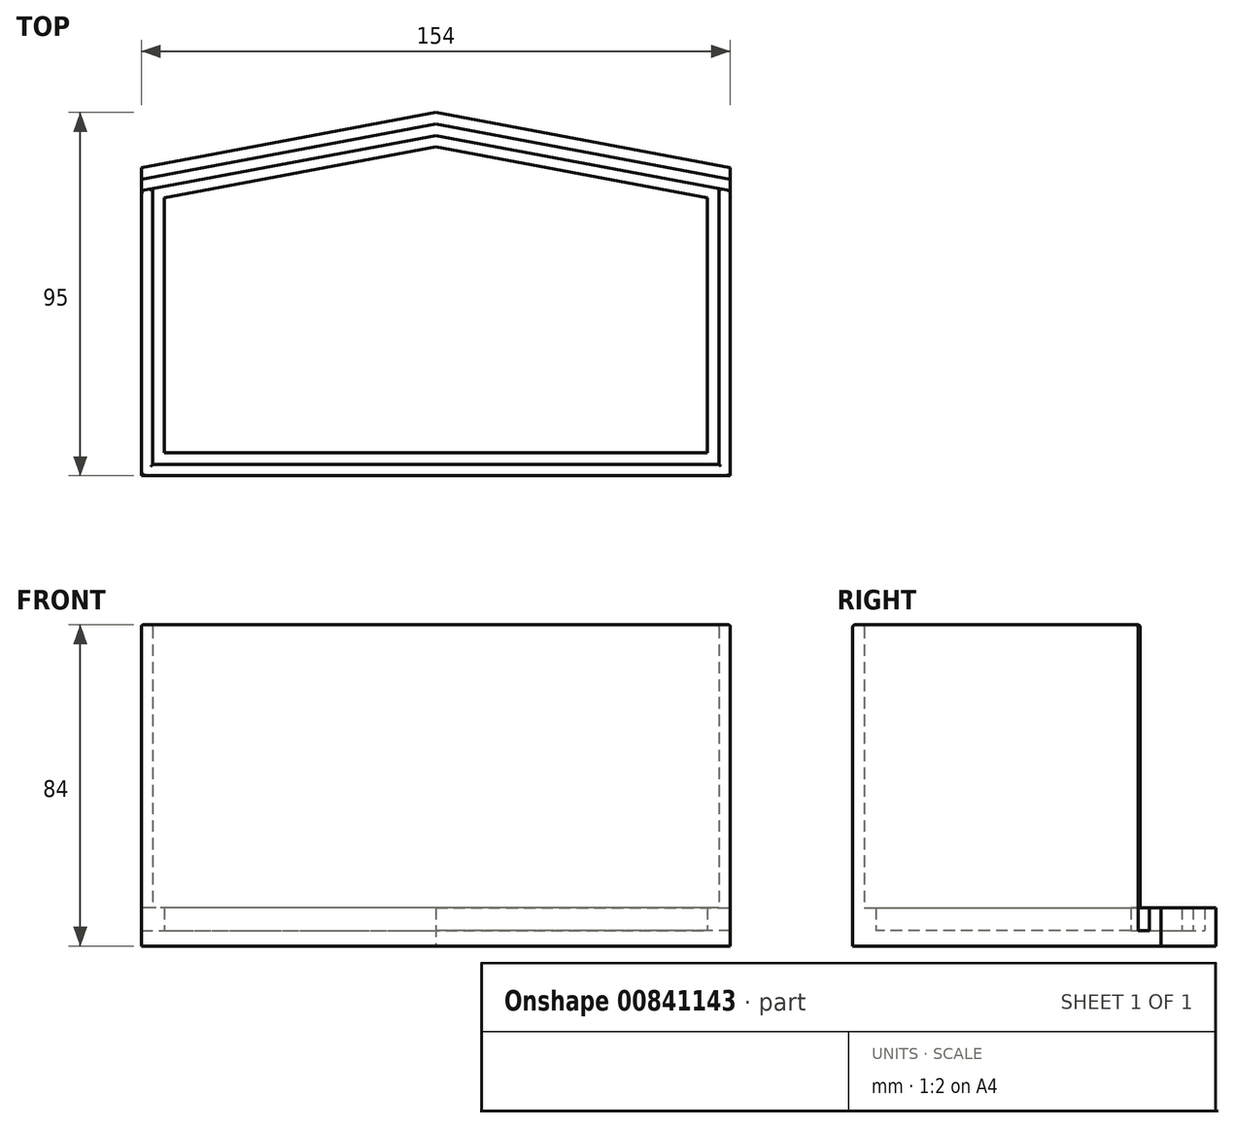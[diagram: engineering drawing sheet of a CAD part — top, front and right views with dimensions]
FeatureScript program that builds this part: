
annotation { "Feature Type Name" : "Feature", "Feature Type Description" : "" }
export const myFeature = defineFeature(function(context is Context, id is Id, definition is map)
    precondition{}
    {
        {
            var Q0;
            Q0=qCreatedBy(makeId("Top.planeOp"),FACE);
            var sketch = newSketch(context, id + "F0", { "sketchPlane" : qUnion([Q0])});
            skLineSegment(sketch, "E0.bottom", {"start": v(80, -49) * mm, "end": v(-80, -49) * mm});
            skLineSegment(sketch, "E0.top", {"start": v(80, 49) * mm, "end": v(-80, 49) * mm, "construction": true});
            skLineSegment(sketch, "E0.left", {"start": v(80, -49) * mm, "end": v(80, 49) * mm});
            skLineSegment(sketch, "E0.right", {"start": v(-80, -49) * mm, "end": v(-80, 49) * mm});
            skPoint(sketch, "E0.middle", {"position": v(0, 0) * mm});
            skLineSegment(sketch, "E1.bottom", {"start": v(-80, -49) * mm, "end": v(80, -49) * mm});
            skLineSegment(sketch, "E1.left", {"start": v(-80, -49) * mm, "end": v(-80, 85) * mm});
            skLineSegment(sketch, "E1.right", {"start": v(80, -49) * mm, "end": v(80, 43) * mm});
            skLineSegment(sketch, "E2.bottom", {"start": v(77, -46) * mm, "end": v(-77, -46) * mm});
            skLineSegment(sketch, "E2.top", {"start": v(77, 46) * mm, "end": v(-77, 46) * mm, "construction": true});
            skLineSegment(sketch, "E2.left", {"start": v(77, -46) * mm, "end": v(77, 46) * mm});
            skLineSegment(sketch, "E2.right", {"start": v(-77, -46) * mm, "end": v(-77, 46) * mm});
            skLineSegment(sketch, "E3.bottom", {"start": v(74, -43) * mm, "end": v(-74, -43) * mm});
            skLineSegment(sketch, "E3.top", {"start": v(74, 43) * mm, "end": v(-74, 43) * mm, "construction": true});
            skLineSegment(sketch, "E3.left", {"start": v(74, -43) * mm, "end": v(74, 43) * mm});
            skLineSegment(sketch, "E3.right", {"start": v(-74, -43) * mm, "end": v(-74, 43) * mm});
            skLineSegment(sketch, "E4.bottom", {"start": v(71, -40) * mm, "end": v(-71, -40) * mm});
            skLineSegment(sketch, "E4.top", {"start": v(71, 40) * mm, "end": v(-71, 40) * mm, "construction": true});
            skLineSegment(sketch, "E4.left", {"start": v(71, -40) * mm, "end": v(71, 40) * mm});
            skLineSegment(sketch, "E4.right", {"start": v(-71, -40) * mm, "end": v(-71, 40) * mm});
            skLineSegment(sketch, "E5.bottom", {"start": v(-80, 49) * mm, "end": v(80, 49) * mm, "construction": true});
            skLineSegment(sketch, "E5.top", {"start": v(-80, 34) * mm, "end": v(80, 34) * mm, "construction": true});
            skLineSegment(sketch, "E5.left", {"start": v(-80, 49) * mm, "end": v(-80, 34) * mm, "construction": true});
            skLineSegment(sketch, "E5.right", {"start": v(80, 49) * mm, "end": v(80, 34) * mm, "construction": true});
            skLineSegment(sketch, "E6", {"start": v(0, 49) * mm, "end": v(0, -49) * mm, "construction": true});
            skLineSegment(sketch, "E7", {"start": v(0, 49) * mm, "end": v(-80, 34) * mm});
            skLineSegment(sketch, "E8", {"start": v(0, 46) * mm, "end": v(-80, 31) * mm});
            skLineSegment(sketch, "E9", {"start": v(0, 43) * mm, "end": v(-80, 28) * mm});
            skLineSegment(sketch, "E10", {"start": v(0, 40) * mm, "end": v(-80, 25) * mm});
            skLineSegment(sketch, "E11", {"start": v(0, 49) * mm, "end": v(80, 34) * mm});
            skLineSegment(sketch, "E12", {"start": v(0, 46) * mm, "end": v(80, 31) * mm});
            skLineSegment(sketch, "E13", {"start": v(0, 43) * mm, "end": v(80, 28) * mm});
            skLineSegment(sketch, "E14", {"start": v(0, 40) * mm, "end": v(80, 25) * mm});
            skSolve(sketch);
        }
        {
            var Q0;
            {var subQ6=sQuery(id+"F0.wireOp",EDGE,"E4.bottom");Q0=makeQuery(id+"F0.imprint","IMPRINT",FACE,{"disambiguationData":[TD([[makeQuery(id+"F0.imprint","IMPRINT",EDGE,{"derivedFrom":subQ6}),-1.0]])]});}
            var Q1;
            {var subQ2=sQuery(id+"F0.wireOp",EDGE,"E2.bottom");Q1=makeQuery(id+"F0.imprint","IMPRINT",FACE,{"disambiguationData":[TD([[makeQuery(id+"F0.imprint","IMPRINT",EDGE,{"derivedFrom":subQ2}),-1.0]])]});}
            var Q2;
            {var subQ0=sQuery(id+"F0.wireOp",EDGE,"E13");var subQ9=sQuery(id+"F0.wireOp",EDGE,"E4.left");var subQ11=makeQuery(id+"F0.imprint","INTERSECT",VERTEX,{"derivedFrom":[subQ9,subQ0]});Q2=makeQuery(id+"F0.imprint","IMPRINT",FACE,{"disambiguationData":[TD([[makeQuery(id+"F0.imprint","IMPRINT",EDGE,{"disambiguationData":[TD([[subQ11,-1.0]])],"derivedFrom":subQ9}),1.0]])]});}
            var Q3;
            {var subQ2=sQuery(id+"F0.wireOp",EDGE,"E1.bottom");Q3=makeQuery(id+"F0.imprint","IMPRINT",FACE,{"disambiguationData":[TD([[makeQuery(id+"F0.imprint","IMPRINT",EDGE,{"derivedFrom":subQ2}),1.0]])]});}
            var Q4;
            {var subQ7=sQuery(id+"F0.wireOp",EDGE,"E3.bottom");Q4=makeQuery(id+"F0.imprint","IMPRINT",FACE,{"disambiguationData":[TD([[makeQuery(id+"F0.imprint","IMPRINT",EDGE,{"derivedFrom":subQ7}),-1.0]])]});}
            var Q5;
            {var subQ0=sQuery(id+"F0.wireOp",EDGE,"E8");var subQ1=sQuery(id+"F0.wireOp",EDGE,"E1.left");var subQ2=makeQuery(id+"F0.imprint","INTERSECT",VERTEX,{"derivedFrom":[subQ1,subQ0]});Q5=makeQuery(id+"F0.imprint","IMPRINT",FACE,{"disambiguationData":[TD([[makeQuery(id+"F0.imprint","IMPRINT",EDGE,{"disambiguationData":[TD([[subQ2,1.0]])],"derivedFrom":subQ1}),-1.0]])]});}
            var Q6;
            {var subQ0=sQuery(id+"F0.wireOp",EDGE,"E7");var subQ1=sQuery(id+"F0.wireOp",EDGE,"E1.left");var subQ2=makeQuery(id+"F0.imprint","INTERSECT",VERTEX,{"derivedFrom":[subQ1,subQ0]});Q6=makeQuery(id+"F0.imprint","IMPRINT",FACE,{"disambiguationData":[TD([[makeQuery(id+"F0.imprint","IMPRINT",EDGE,{"disambiguationData":[TD([[subQ2,1.0]])],"derivedFrom":subQ1}),-1.0]])]});}
            var Q7;
            {var subQ0=sQuery(id+"F0.wireOp",EDGE,"E9");var subQ1=sQuery(id+"F0.wireOp",EDGE,"E1.left");var subQ2=makeQuery(id+"F0.imprint","INTERSECT",VERTEX,{"derivedFrom":[subQ1,subQ0]});Q7=makeQuery(id+"F0.imprint","IMPRINT",FACE,{"disambiguationData":[TD([[makeQuery(id+"F0.imprint","IMPRINT",EDGE,{"disambiguationData":[TD([[subQ2,1.0]])],"derivedFrom":subQ1}),-1.0]])]});}
            var Q8;
            {var subQ0=sQuery(id+"F0.wireOp",EDGE,"E7");var subQ1=sQuery(id+"F0.wireOp",EDGE,"E2.right");var subQ2=makeQuery(id+"F0.imprint","INTERSECT",VERTEX,{"derivedFrom":[subQ1,subQ0]});Q8=makeQuery(id+"F0.imprint","IMPRINT",FACE,{"disambiguationData":[TD([[makeQuery(id+"F0.imprint","IMPRINT",EDGE,{"disambiguationData":[TD([[subQ2,1.0]])],"derivedFrom":subQ1}),-1.0]])]});}
            var Q9;
            {var subQ0=sQuery(id+"F0.wireOp",EDGE,"E9");var subQ1=sQuery(id+"F0.wireOp",EDGE,"E2.right");var subQ2=makeQuery(id+"F0.imprint","INTERSECT",VERTEX,{"derivedFrom":[subQ1,subQ0]});Q9=makeQuery(id+"F0.imprint","IMPRINT",FACE,{"disambiguationData":[TD([[makeQuery(id+"F0.imprint","IMPRINT",EDGE,{"disambiguationData":[TD([[subQ2,-1.0]])],"derivedFrom":subQ1}),-1.0]])]});}
            var Q10;
            {var subQ0=sQuery(id+"F0.wireOp",EDGE,"E10");var subQ1=sQuery(id+"F0.wireOp",EDGE,"E2.right");var subQ2=makeQuery(id+"F0.imprint","INTERSECT",VERTEX,{"derivedFrom":[subQ1,subQ0]});Q10=makeQuery(id+"F0.imprint","IMPRINT",FACE,{"disambiguationData":[TD([[makeQuery(id+"F0.imprint","IMPRINT",EDGE,{"disambiguationData":[TD([[subQ2,-1.0]])],"derivedFrom":subQ1}),-1.0]])]});}
            var Q11;
            {var subQ0=sQuery(id+"F0.wireOp",EDGE,"E9");var subQ1=sQuery(id+"F0.wireOp",EDGE,"E3.right");var subQ2=makeQuery(id+"F0.imprint","INTERSECT",VERTEX,{"derivedFrom":[subQ1,subQ0]});Q11=makeQuery(id+"F0.imprint","IMPRINT",FACE,{"disambiguationData":[TD([[makeQuery(id+"F0.imprint","IMPRINT",EDGE,{"disambiguationData":[TD([[subQ2,-1.0]])],"derivedFrom":subQ1}),-1.0]])]});}
            var Q12;
            {var subQ0=sQuery(id+"F0.wireOp",EDGE,"E10");var subQ1=sQuery(id+"F0.wireOp",EDGE,"E3.right");var subQ2=makeQuery(id+"F0.imprint","INTERSECT",VERTEX,{"derivedFrom":[subQ1,subQ0]});Q12=makeQuery(id+"F0.imprint","IMPRINT",FACE,{"disambiguationData":[TD([[makeQuery(id+"F0.imprint","IMPRINT",EDGE,{"disambiguationData":[TD([[subQ2,-1.0]])],"derivedFrom":subQ1}),-1.0]])]});}
            var Q13;
            {var subQ0=sQuery(id+"F0.wireOp",EDGE,"E7");var subQ1=sQuery(id+"F0.wireOp",EDGE,"E3.right");var subQ2=makeQuery(id+"F0.imprint","INTERSECT",VERTEX,{"derivedFrom":[subQ1,subQ0]});Q13=makeQuery(id+"F0.imprint","IMPRINT",FACE,{"disambiguationData":[TD([[makeQuery(id+"F0.imprint","IMPRINT",EDGE,{"disambiguationData":[TD([[subQ2,1.0]])],"derivedFrom":subQ1}),-1.0]])]});}
            var Q14;
            {var subQ7=sQuery(id+"F0.wireOp",EDGE,"E11");var subQ9=sQuery(id+"F0.wireOp",EDGE,"E4.left");var subQ10=makeQuery(id+"F0.imprint","INTERSECT",VERTEX,{"derivedFrom":[subQ9,subQ7]});Q14=makeQuery(id+"F0.imprint","IMPRINT",FACE,{"disambiguationData":[TD([[makeQuery(id+"F0.imprint","IMPRINT",EDGE,{"disambiguationData":[TD([[subQ10,1.0]])],"derivedFrom":subQ9}),1.0]])]});}
            var Q15;
            {var subQ0=sQuery(id+"F0.wireOp",EDGE,"E14");var subQ9=sQuery(id+"F0.wireOp",EDGE,"E4.left");var subQ10=makeQuery(id+"F0.imprint","INTERSECT",VERTEX,{"derivedFrom":[subQ9,subQ0]});Q15=makeQuery(id+"F0.imprint","IMPRINT",FACE,{"disambiguationData":[TD([[makeQuery(id+"F0.imprint","IMPRINT",EDGE,{"disambiguationData":[TD([[subQ10,-1.0]])],"derivedFrom":subQ9}),1.0]])]});}
            var Q16;
            {var subQ0=sQuery(id+"F0.wireOp",EDGE,"E11");var subQ1=sQuery(id+"F0.wireOp",EDGE,"E3.left");var subQ2=makeQuery(id+"F0.imprint","INTERSECT",VERTEX,{"derivedFrom":[subQ1,subQ0]});Q16=makeQuery(id+"F0.imprint","IMPRINT",FACE,{"disambiguationData":[TD([[makeQuery(id+"F0.imprint","IMPRINT",EDGE,{"disambiguationData":[TD([[subQ2,1.0]])],"derivedFrom":subQ1}),1.0]])]});}
            var Q17;
            {var subQ0=sQuery(id+"F0.wireOp",EDGE,"E11");var subQ1=sQuery(id+"F0.wireOp",EDGE,"E2.left");var subQ2=makeQuery(id+"F0.imprint","INTERSECT",VERTEX,{"derivedFrom":[subQ1,subQ0]});Q17=makeQuery(id+"F0.imprint","IMPRINT",FACE,{"disambiguationData":[TD([[makeQuery(id+"F0.imprint","IMPRINT",EDGE,{"disambiguationData":[TD([[subQ2,1.0]])],"derivedFrom":subQ1}),1.0]])]});}
            var Q18;
            {var subQ0=sQuery(id+"F0.wireOp",EDGE,"E11");var subQ1=sQuery(id+"F0.wireOp",EDGE,"E1.right");var subQ2=makeQuery(id+"F0.imprint","INTERSECT",VERTEX,{"derivedFrom":[subQ1,subQ0]});Q18=makeQuery(id+"F0.imprint","IMPRINT",FACE,{"disambiguationData":[TD([[makeQuery(id+"F0.imprint","IMPRINT",EDGE,{"disambiguationData":[TD([[subQ2,1.0]])],"derivedFrom":subQ1}),1.0]])]});}
            var Q19;
            {var subQ0=sQuery(id+"F0.wireOp",EDGE,"E12");var subQ1=sQuery(id+"F0.wireOp",EDGE,"E1.right");var subQ2=makeQuery(id+"F0.imprint","INTERSECT",VERTEX,{"derivedFrom":[subQ1,subQ0]});Q19=makeQuery(id+"F0.imprint","IMPRINT",FACE,{"disambiguationData":[TD([[makeQuery(id+"F0.imprint","IMPRINT",EDGE,{"disambiguationData":[TD([[subQ2,1.0]])],"derivedFrom":subQ1}),1.0]])]});}
            var Q20;
            {var subQ0=sQuery(id+"F0.wireOp",EDGE,"E13");var subQ1=sQuery(id+"F0.wireOp",EDGE,"E1.right");var subQ2=makeQuery(id+"F0.imprint","INTERSECT",VERTEX,{"derivedFrom":[subQ1,subQ0]});Q20=makeQuery(id+"F0.imprint","IMPRINT",FACE,{"disambiguationData":[TD([[makeQuery(id+"F0.imprint","IMPRINT",EDGE,{"disambiguationData":[TD([[subQ2,1.0]])],"derivedFrom":subQ1}),1.0]])]});}
            var Q21;
            {var subQ0=sQuery(id+"F0.wireOp",EDGE,"E14");var subQ1=sQuery(id+"F0.wireOp",EDGE,"E2.left");var subQ2=makeQuery(id+"F0.imprint","INTERSECT",VERTEX,{"derivedFrom":[subQ1,subQ0]});Q21=makeQuery(id+"F0.imprint","IMPRINT",FACE,{"disambiguationData":[TD([[makeQuery(id+"F0.imprint","IMPRINT",EDGE,{"disambiguationData":[TD([[subQ2,-1.0]])],"derivedFrom":subQ1}),1.0]])]});}
            var Q22;
            {var subQ0=sQuery(id+"F0.wireOp",EDGE,"E14");var subQ1=sQuery(id+"F0.wireOp",EDGE,"E3.left");var subQ2=makeQuery(id+"F0.imprint","INTERSECT",VERTEX,{"derivedFrom":[subQ1,subQ0]});Q22=makeQuery(id+"F0.imprint","IMPRINT",FACE,{"disambiguationData":[TD([[makeQuery(id+"F0.imprint","IMPRINT",EDGE,{"disambiguationData":[TD([[subQ2,-1.0]])],"derivedFrom":subQ1}),1.0]])]});}
            var Q23;
            {var subQ0=sQuery(id+"F0.wireOp",EDGE,"E13");var subQ1=sQuery(id+"F0.wireOp",EDGE,"E3.left");var subQ2=makeQuery(id+"F0.imprint","INTERSECT",VERTEX,{"derivedFrom":[subQ1,subQ0]});Q23=makeQuery(id+"F0.imprint","IMPRINT",FACE,{"disambiguationData":[TD([[makeQuery(id+"F0.imprint","IMPRINT",EDGE,{"disambiguationData":[TD([[subQ2,-1.0]])],"derivedFrom":subQ1}),1.0]])]});}
            var Q24;
            {var subQ0=sQuery(id+"F0.wireOp",EDGE,"E13");var subQ1=sQuery(id+"F0.wireOp",EDGE,"E2.left");var subQ2=makeQuery(id+"F0.imprint","INTERSECT",VERTEX,{"derivedFrom":[subQ1,subQ0]});Q24=makeQuery(id+"F0.imprint","IMPRINT",FACE,{"disambiguationData":[TD([[makeQuery(id+"F0.imprint","IMPRINT",EDGE,{"disambiguationData":[TD([[subQ2,-1.0]])],"derivedFrom":subQ1}),1.0]])]});}
            extrude(context, id + "F1", {"entities" : qUnion([Q0, Q1, Q2, Q3, Q4, Q5, Q6, Q7, Q8, Q9, Q10, Q11, Q12, Q13, Q14, Q15, Q16, Q17, Q18, Q19, Q20, Q21, Q22, Q23, Q24]), "depth" : 4 * mm, "offsetDistance" : 25 * mm});
        }
        {
            var Q0;
            {var subQ0=sQuery(id+"F0.wireOp",EDGE,"E11");var subQ1=sQuery(id+"F0.wireOp",EDGE,"E1.right");var subQ2=makeQuery(id+"F0.imprint","INTERSECT",VERTEX,{"derivedFrom":[subQ1,subQ0]});Q0=makeQuery(id+"F0.imprint","IMPRINT",FACE,{"disambiguationData":[TD([[makeQuery(id+"F0.imprint","IMPRINT",EDGE,{"disambiguationData":[TD([[subQ2,1.0]])],"derivedFrom":subQ1}),1.0]])]});}
            var Q1;
            {var subQ0=sQuery(id+"F0.wireOp",EDGE,"E11");var subQ1=sQuery(id+"F0.wireOp",EDGE,"E2.left");var subQ2=makeQuery(id+"F0.imprint","INTERSECT",VERTEX,{"derivedFrom":[subQ1,subQ0]});Q1=makeQuery(id+"F0.imprint","IMPRINT",FACE,{"disambiguationData":[TD([[makeQuery(id+"F0.imprint","IMPRINT",EDGE,{"disambiguationData":[TD([[subQ2,1.0]])],"derivedFrom":subQ1}),1.0]])]});}
            var Q2;
            {var subQ0=sQuery(id+"F0.wireOp",EDGE,"E11");var subQ1=sQuery(id+"F0.wireOp",EDGE,"E3.left");var subQ2=makeQuery(id+"F0.imprint","INTERSECT",VERTEX,{"derivedFrom":[subQ1,subQ0]});Q2=makeQuery(id+"F0.imprint","IMPRINT",FACE,{"disambiguationData":[TD([[makeQuery(id+"F0.imprint","IMPRINT",EDGE,{"disambiguationData":[TD([[subQ2,1.0]])],"derivedFrom":subQ1}),1.0]])]});}
            var Q3;
            {var subQ7=sQuery(id+"F0.wireOp",EDGE,"E11");var subQ9=sQuery(id+"F0.wireOp",EDGE,"E4.left");var subQ10=makeQuery(id+"F0.imprint","INTERSECT",VERTEX,{"derivedFrom":[subQ9,subQ7]});Q3=makeQuery(id+"F0.imprint","IMPRINT",FACE,{"disambiguationData":[TD([[makeQuery(id+"F0.imprint","IMPRINT",EDGE,{"disambiguationData":[TD([[subQ10,1.0]])],"derivedFrom":subQ9}),1.0]])]});}
            var Q4;
            {var subQ0=sQuery(id+"F0.wireOp",EDGE,"E7");var subQ1=sQuery(id+"F0.wireOp",EDGE,"E3.right");var subQ2=makeQuery(id+"F0.imprint","INTERSECT",VERTEX,{"derivedFrom":[subQ1,subQ0]});Q4=makeQuery(id+"F0.imprint","IMPRINT",FACE,{"disambiguationData":[TD([[makeQuery(id+"F0.imprint","IMPRINT",EDGE,{"disambiguationData":[TD([[subQ2,1.0]])],"derivedFrom":subQ1}),-1.0]])]});}
            var Q5;
            {var subQ0=sQuery(id+"F0.wireOp",EDGE,"E7");var subQ1=sQuery(id+"F0.wireOp",EDGE,"E2.right");var subQ2=makeQuery(id+"F0.imprint","INTERSECT",VERTEX,{"derivedFrom":[subQ1,subQ0]});Q5=makeQuery(id+"F0.imprint","IMPRINT",FACE,{"disambiguationData":[TD([[makeQuery(id+"F0.imprint","IMPRINT",EDGE,{"disambiguationData":[TD([[subQ2,1.0]])],"derivedFrom":subQ1}),-1.0]])]});}
            var Q6;
            {var subQ0=sQuery(id+"F0.wireOp",EDGE,"E7");var subQ1=sQuery(id+"F0.wireOp",EDGE,"E1.left");var subQ2=makeQuery(id+"F0.imprint","INTERSECT",VERTEX,{"derivedFrom":[subQ1,subQ0]});Q6=makeQuery(id+"F0.imprint","IMPRINT",FACE,{"disambiguationData":[TD([[makeQuery(id+"F0.imprint","IMPRINT",EDGE,{"disambiguationData":[TD([[subQ2,1.0]])],"derivedFrom":subQ1}),-1.0]])]});}
            var Q7;
            {var subQ0=sQuery(id+"F0.wireOp",EDGE,"E9");var subQ1=sQuery(id+"F0.wireOp",EDGE,"E1.left");var subQ2=makeQuery(id+"F0.imprint","INTERSECT",VERTEX,{"derivedFrom":[subQ1,subQ0]});Q7=makeQuery(id+"F0.imprint","IMPRINT",FACE,{"disambiguationData":[TD([[makeQuery(id+"F0.imprint","IMPRINT",EDGE,{"disambiguationData":[TD([[subQ2,1.0]])],"derivedFrom":subQ1}),-1.0]])]});}
            var Q8;
            {var subQ0=sQuery(id+"F0.wireOp",EDGE,"E10");var subQ1=sQuery(id+"F0.wireOp",EDGE,"E2.right");var subQ2=makeQuery(id+"F0.imprint","INTERSECT",VERTEX,{"derivedFrom":[subQ1,subQ0]});Q8=makeQuery(id+"F0.imprint","IMPRINT",FACE,{"disambiguationData":[TD([[makeQuery(id+"F0.imprint","IMPRINT",EDGE,{"disambiguationData":[TD([[subQ2,-1.0]])],"derivedFrom":subQ1}),-1.0]])]});}
            var Q9;
            {var subQ0=sQuery(id+"F0.wireOp",EDGE,"E10");var subQ1=sQuery(id+"F0.wireOp",EDGE,"E3.right");var subQ2=makeQuery(id+"F0.imprint","INTERSECT",VERTEX,{"derivedFrom":[subQ1,subQ0]});Q9=makeQuery(id+"F0.imprint","IMPRINT",FACE,{"disambiguationData":[TD([[makeQuery(id+"F0.imprint","IMPRINT",EDGE,{"disambiguationData":[TD([[subQ2,-1.0]])],"derivedFrom":subQ1}),-1.0]])]});}
            var Q10;
            {var subQ0=sQuery(id+"F0.wireOp",EDGE,"E14");var subQ9=sQuery(id+"F0.wireOp",EDGE,"E4.left");var subQ10=makeQuery(id+"F0.imprint","INTERSECT",VERTEX,{"derivedFrom":[subQ9,subQ0]});Q10=makeQuery(id+"F0.imprint","IMPRINT",FACE,{"disambiguationData":[TD([[makeQuery(id+"F0.imprint","IMPRINT",EDGE,{"disambiguationData":[TD([[subQ10,-1.0]])],"derivedFrom":subQ9}),1.0]])]});}
            var Q11;
            {var subQ0=sQuery(id+"F0.wireOp",EDGE,"E13");var subQ1=sQuery(id+"F0.wireOp",EDGE,"E1.right");var subQ2=makeQuery(id+"F0.imprint","INTERSECT",VERTEX,{"derivedFrom":[subQ1,subQ0]});Q11=makeQuery(id+"F0.imprint","IMPRINT",FACE,{"disambiguationData":[TD([[makeQuery(id+"F0.imprint","IMPRINT",EDGE,{"disambiguationData":[TD([[subQ2,1.0]])],"derivedFrom":subQ1}),1.0]])]});}
            var Q12;
            {var subQ0=sQuery(id+"F0.wireOp",EDGE,"E14");var subQ1=sQuery(id+"F0.wireOp",EDGE,"E2.left");var subQ2=makeQuery(id+"F0.imprint","INTERSECT",VERTEX,{"derivedFrom":[subQ1,subQ0]});Q12=makeQuery(id+"F0.imprint","IMPRINT",FACE,{"disambiguationData":[TD([[makeQuery(id+"F0.imprint","IMPRINT",EDGE,{"disambiguationData":[TD([[subQ2,-1.0]])],"derivedFrom":subQ1}),1.0]])]});}
            var Q13;
            {var subQ0=sQuery(id+"F0.wireOp",EDGE,"E14");var subQ1=sQuery(id+"F0.wireOp",EDGE,"E3.left");var subQ2=makeQuery(id+"F0.imprint","INTERSECT",VERTEX,{"derivedFrom":[subQ1,subQ0]});Q13=makeQuery(id+"F0.imprint","IMPRINT",FACE,{"disambiguationData":[TD([[makeQuery(id+"F0.imprint","IMPRINT",EDGE,{"disambiguationData":[TD([[subQ2,-1.0]])],"derivedFrom":subQ1}),1.0]])]});}
            var Q14;
            {var subQ2=sQuery(id+"F0.wireOp",EDGE,"E1.bottom");Q14=makeQuery(id+"F0.imprint","IMPRINT",FACE,{"disambiguationData":[TD([[makeQuery(id+"F0.imprint","IMPRINT",EDGE,{"derivedFrom":subQ2}),1.0]])]});}
            var Q15;
            {var subQ7=sQuery(id+"F0.wireOp",EDGE,"E3.bottom");Q15=makeQuery(id+"F0.imprint","IMPRINT",FACE,{"disambiguationData":[TD([[makeQuery(id+"F0.imprint","IMPRINT",EDGE,{"derivedFrom":subQ7}),-1.0]])]});}
            var Q16;
            {var subQ0=sQuery(id+"F0.wireOp",EDGE,"E8");var subQ1=sQuery(id+"F0.wireOp",EDGE,"E1.left");var subQ2=makeQuery(id+"F0.imprint","INTERSECT",VERTEX,{"derivedFrom":[subQ1,subQ0]});Q16=makeQuery(id+"F0.imprint","IMPRINT",FACE,{"disambiguationData":[TD([[makeQuery(id+"F0.imprint","IMPRINT",EDGE,{"disambiguationData":[TD([[subQ2,1.0]])],"derivedFrom":subQ1}),-1.0]])]});}
            var Q17;
            {var subQ0=sQuery(id+"F0.wireOp",EDGE,"E12");var subQ1=sQuery(id+"F0.wireOp",EDGE,"E1.right");var subQ2=makeQuery(id+"F0.imprint","INTERSECT",VERTEX,{"derivedFrom":[subQ1,subQ0]});Q17=makeQuery(id+"F0.imprint","IMPRINT",FACE,{"disambiguationData":[TD([[makeQuery(id+"F0.imprint","IMPRINT",EDGE,{"disambiguationData":[TD([[subQ2,1.0]])],"derivedFrom":subQ1}),1.0]])]});}
            extrude(context, id + "F2", {"entities" : qUnion([Q0, Q1, Q2, Q3, Q4, Q5, Q6, Q7, Q8, Q9, Q10, Q11, Q12, Q13, Q14, Q15, Q16, Q17]), "operationType" : NewBodyOperationType.ADD, "depth" : 10 * mm, "offsetDistance" : 25 * mm});
        }
        {
            var Q0;
            {var subQ2=sQuery(id+"F0.wireOp",EDGE,"E2.bottom");Q0=makeQuery(id+"F0.imprint","IMPRINT",FACE,{"disambiguationData":[TD([[makeQuery(id+"F0.imprint","IMPRINT",EDGE,{"derivedFrom":subQ2}),-1.0]])]});}
            var Q1;
            {var subQ0=sQuery(id+"F0.wireOp",EDGE,"E10");var subQ1=sQuery(id+"F0.wireOp",EDGE,"E2.right");var subQ2=makeQuery(id+"F0.imprint","INTERSECT",VERTEX,{"derivedFrom":[subQ1,subQ0]});Q1=makeQuery(id+"F0.imprint","IMPRINT",FACE,{"disambiguationData":[TD([[makeQuery(id+"F0.imprint","IMPRINT",EDGE,{"disambiguationData":[TD([[subQ2,-1.0]])],"derivedFrom":subQ1}),-1.0]])]});}
            var Q2;
            {var subQ0=sQuery(id+"F0.wireOp",EDGE,"E14");var subQ1=sQuery(id+"F0.wireOp",EDGE,"E2.left");var subQ2=makeQuery(id+"F0.imprint","INTERSECT",VERTEX,{"derivedFrom":[subQ1,subQ0]});Q2=makeQuery(id+"F0.imprint","IMPRINT",FACE,{"disambiguationData":[TD([[makeQuery(id+"F0.imprint","IMPRINT",EDGE,{"disambiguationData":[TD([[subQ2,-1.0]])],"derivedFrom":subQ1}),1.0]])]});}
            extrude(context, id + "F3", {"entities" : qUnion([Q0, Q1, Q2]), "operationType" : NewBodyOperationType.ADD, "depth" : 84 * mm, "offsetDistance" : 25 * mm});
        }
        {
            var Q0;
            Q0=makeQuery(id+"F3.opExtrude","CAP_FACE",FACE,{"disambiguationData":[OSD([sQuery(id+"F0.wireOp",EDGE,"E2.bottom"),sQuery(id+"F0.wireOp",EDGE,"E2.left"),sQuery(id+"F0.wireOp",EDGE,"E2.right"),sQuery(id+"F0.wireOp",EDGE,"E3.bottom"),sQuery(id+"F0.wireOp",EDGE,"E3.left"),sQuery(id+"F0.wireOp",EDGE,"E3.right"),sQuery(id+"F0.wireOp",EDGE,"E10"),sQuery(id+"F0.wireOp",EDGE,"E14")])],"isStart":false});
            fillet(context, id + "F4", {"entities" : qUnion([Q0]), "radius" : .5 * mm, "tangentPropagation" : true, "allowEdgeOverflow" : false});
        }
    });
